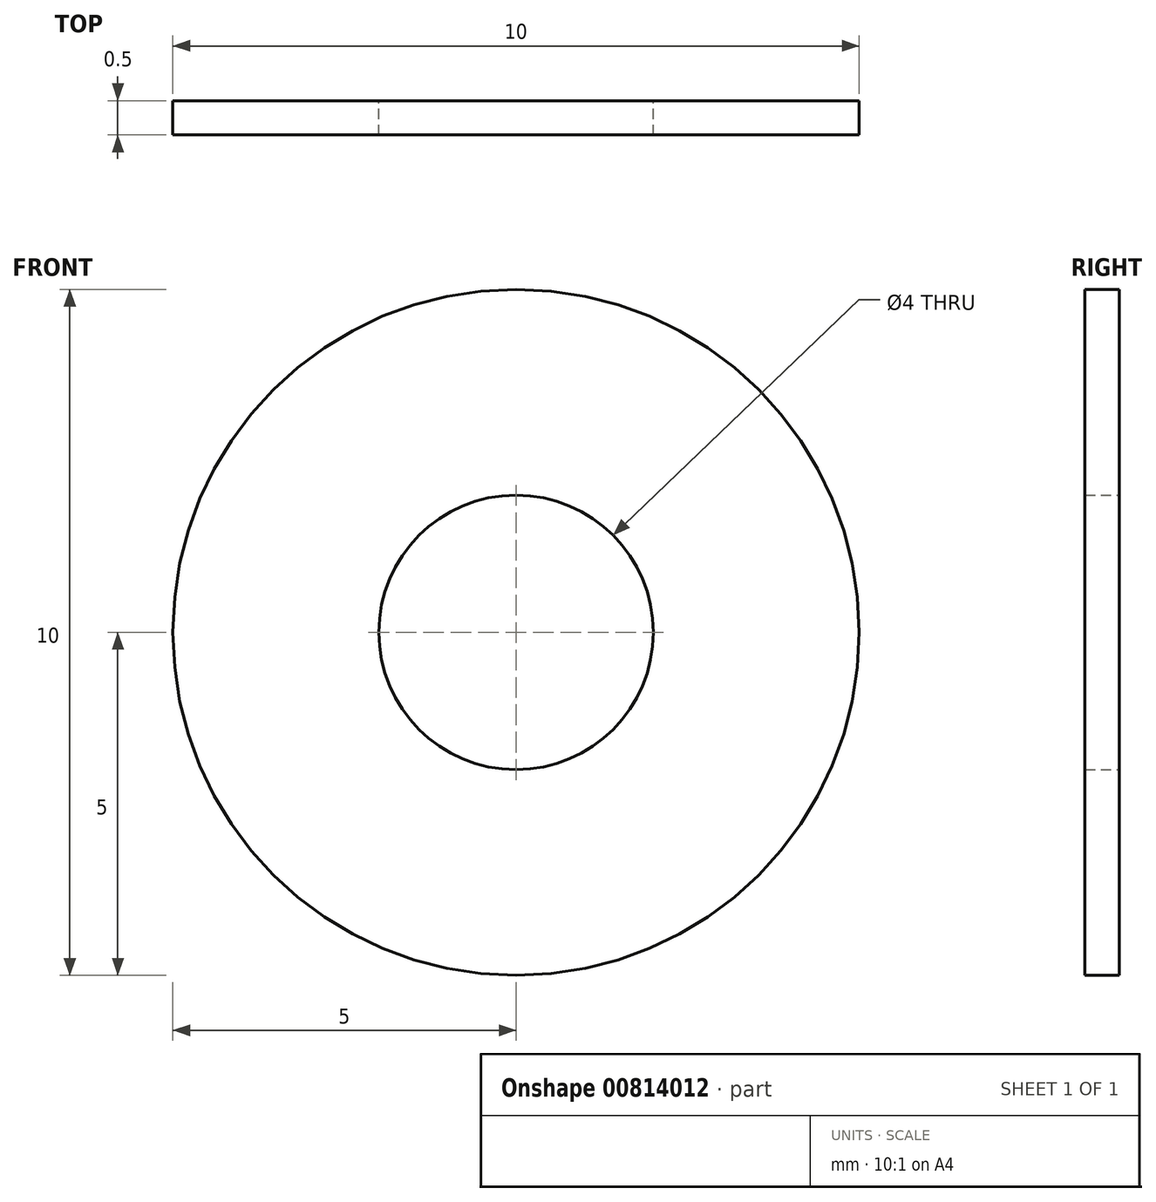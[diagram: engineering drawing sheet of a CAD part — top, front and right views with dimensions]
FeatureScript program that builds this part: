
annotation { "Feature Type Name" : "Feature", "Feature Type Description" : "" }
export const myFeature = defineFeature(function(context is Context, id is Id, definition is map)
    precondition{}
    {
        {
            var Q0;
            Q0=qCreatedBy(makeId("Front.planeOp"),FACE);
            var sketch = newSketch(context, id + "F0", { "sketchPlane" : qUnion([Q0])});
            skCircle(sketch, "E0", {"center": v(0, 0) * mm, "radius": 2 * mm});
            skCircle(sketch, "E1", {"center": v(0, 0) * mm, "radius": 5 * mm});
            skSolve(sketch);
        }
        {
            var Q0;
            Q0=qSketchRegion(id+"F0",true);
            extrude(context, id + "F1", {"entities" : qUnion([Q0]), "depth" : .5 * mm, "offsetDistance" : 25 * mm});
        }
    });
